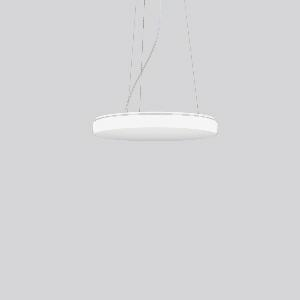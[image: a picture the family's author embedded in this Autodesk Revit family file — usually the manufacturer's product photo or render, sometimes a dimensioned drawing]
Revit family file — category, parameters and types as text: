
# Revit family: flat_polymero_kreis_slim_312091_002_2_1cb1
name_source: partatom
category: Lighting Fixtures
units: mm (PartAtom-declared; Revit-internal decimal feet)

## family parameters
Cut with Voids When Loaded = No
Host = Face
Light Source = No
Part Type = Normal
Room Calculation Point = No
Round Connector Dimension = Use Diameter
Shared = No

## types (1)
- FLAT POLYMERO KREIS SLIM (1 x LED Modul 830, 3400 lm, 3000)
    Apparent Load = 29 VA
    CIE Flux Codes = 42 73 92 87 100
    Color Rendering = 80
    Color Temperature = 3000
    Default Elevation = 1800 mm
    Description = Series: FLAT POLYMERO KREIS SLIM
Decorative round LED pendant luminaire. Base and canopy: metal, powder-coated, white. Canopy Ø 205 mm, h 35 mm. Diffuser made of plastic (polycarbonate), opal, shockproof. Diffuser fastening: patented push system. Homogeneous and smooth light distribution. Suitable for pendant. 3-point steel cable suspension, steplessly adjustable. Special lengths available on request. 
Colour: white
Diameter: 515 mm
Height: 69 mm
Suspension length: 350-1300 mm
Lamp: LED
Socket: without socket
Colour temperature: 3000K
Colour rendering index (CRI): 83
System power: 29 W
Rated luminous flux: 3400 lm
Luminous efficiency: 117 lm/W
Control gear: AC Strom, dim.Ph.an-/abschnitt
Protection class: I
Type of protection: IP 40
    Height = 69 mm
    Lamp = 1 x LED Modul 830
    Lamp Light Flux = 3400 lm
    Lamp count = 1
    Length = 515 mm
    Lifetime = 50000 h
    Luminous efficacy = 117 lm/W
    Manufacturer = RZB
    ModVariant = No
    Model = 312091.002.2
    Mounting Place = Ceiling
    Mounting Type = Pendant
    Number of Poles = 1
    OnlyDefault = Yes
    Power Factor = 1
    Product Name = FLAT POLYMERO KREIS SLIM
    Product group = Pendant luminaires
    ProductGroupID = 902
    Protection Class = Protection class I
    Protection Degree = IP 40
    RLX_Detail_Level = 1
    RLX_Emergency_Light_Flux = 0 lm
    RLX_Emergency_Type = 0
    RLX_Emergency_Type_DB = No
    RlxData = <blob elided: 42389 chars, md5=0edba46b>
    Socket = socket
    Standby Power = 0 W
    System Light Flux = 3400 lm
    System Power = 29 W
    Type Comments = Product without accessories
    Type Image = 312091.002.jpg
    URL = http://relux.com
    VarID = ---
    Voltage = 230 V
    Voltage Range = 220-240 V
    Weight = 0.00 kg
    Width = 0 mm  [stored 0 ft]

note: [stored X ft] marks values corroborated as IEEE doubles in the binary element streams (Revit-internal decimal feet)

## geometry (parser evidence)
native form markers: Blend x4, Sweep x12
no freeform markers — native parametric forms only
